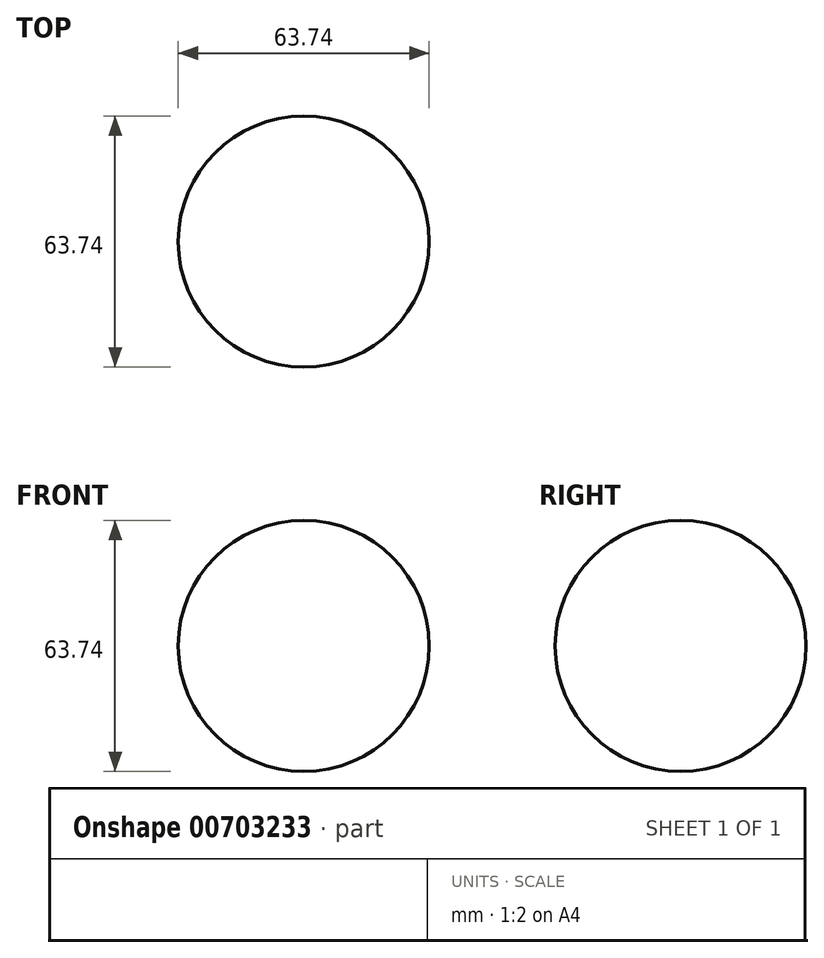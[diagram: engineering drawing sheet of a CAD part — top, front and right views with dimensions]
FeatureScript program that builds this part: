
annotation { "Feature Type Name" : "Feature", "Feature Type Description" : "" }
export const myFeature = defineFeature(function(context is Context, id is Id, definition is map)
    precondition{}
    {
        {
            var Q0;
            Q0=qCreatedBy(makeId("Top.planeOp"),FACE);
            var sketch = newSketch(context, id + "F0", { "sketchPlane" : qUnion([Q0])});
            skCircle(sketch, "E0", {"center": v(0, 0) * mm, "radius": 31.87 * mm});
            skLineSegment(sketch, "E1", {"start": v(0, 31.87) * mm, "end": v(0, -31.87) * mm});
            skSolve(sketch);
        }
        {
            var Q0;
            {var subQ0=sQuery(id+"F0.wireOp",EDGE,"E1");Q0=makeQuery(id+"F0.imprint","IMPRINT",FACE,{"disambiguationData":[TD([[makeQuery(id+"F0.imprint","IMPRINT",EDGE,{"derivedFrom":subQ0}),-1.0]])]});}
            var Q1;
            Q1=sQuery(id+"F0.wireOp",EDGE,"E1");
            revolve(context, id + "F1", {"surfaceOperationType" : NewSurfaceOperationType.NEW, "entities" : qUnion([Q0]), "axis" : qUnion([Q1]), "revolveType" : RevolveType.FULL});
        }
    });
